# Revit family: rondel_41-s_51wd107ag1as
name_source: partatom
category: Lighting Fixtures
units: mm (PartAtom-declared; Revit-internal decimal feet)

## family parameters
Cut with Voids When Loaded = No
Host = Face
Light Source = No
Part Type = Normal
Room Calculation Point = No
Round Connector Dimension = Use Diameter
Shared = No

## types (1)
- --- (1 x LED, 1350 lm, 14 W, 3000K)
    Apparent Load = 14 VA
    CIE Flux Codes = 40 69 88 87 100
    Color Rendering = 80
    Color Temperature = 3000K
    Default Elevation = 1800 mm
    Description = Rondel 41-S, wall and ceiling luminaire, primary optical cover: enclosure, of PMMA, opal, light emission: direct distribution, primary light characteristic: symmetric, installation type: surface-mounted, LED, rated luminous flux: 1.350lm, luminous efficacy: 96lm/W, light colour: 830/840, colour temperature: 3000/4000K, control gear: ECG, with terminal, 3-pole, max. 2.5mm², mains connection: 230V, AC, 50/60Hz, rated input power: 14W, luminaire housing, round, of steel, powder-coated, white, diameter: 280mm, height: 100mm, brightness and presence sensor, HF sensor, protection rating (complete): IP44, insulation class (complete): insulation class I (protective earthing), certification: CE, impact resistance: IK02, permissible operating ambient temperature: -20..+40°C, permissible storage temperature: -30..+80°C, packaging unit: 1 piece
    Height = 100 mm  [stored 0.328084 ft]
    Lamp = 1 x LED
    Lamp Light Flux = 1350 lm
    Lamp Power = 14 W
    Lamp count = 1
    Length = 280 mm
    Luminous efficacy = 96 lm/W
    Manufacturer = Siteco
    ModVariant = No
    Model = 51WD107AG1AS
    Mounting Place = Ceiling
    Mounting Type = Surface mounted
    Number of Poles = 1
    OnlyDefault = Yes
    Power Factor = 1
    Product Name = Rondel 41-S
    Product group = wall and ceiling luminaire
    ProductGroupID = 302
    Protection Class = Protection class I
    Protection Degree = IP 44
    RLX_Detail_Level = 1
    RLX_Emergency_Light_Flux = 0 lm
    RLX_Emergency_Type = 0
    RLX_Emergency_Type_DB = No
    RlxData = <blob elided: 34965 chars, md5=db0b26cf>
    Socket = socket
    Standby Power = 0 W
    System Light Flux = 1350 lm
    System Power = 14 W
    Type Comments = individual setting: colour temperature 3000K, luminous flux: 100 % | (HIGH)
    Type Image = l_1006959.jpg
    URL = http://relux.com
    VarID = @adj_125011
    Voltage = 0 V
    Weight = 0.00 kg
    Width = 0 mm  [stored 0 ft]

note: [stored X ft] marks values corroborated as IEEE doubles in the binary element streams (Revit-internal decimal feet)

## geometry (parser evidence)
native form markers: Blend x4, Sweep x14
no freeform markers — native parametric forms only
